# Revit family: ARRN
name_source: partatom
category: Lighting Fixtures
revit_build: Autodesk Revit 2014 (Build: 20130308_1515(x64)
units: mm (PartAtom-declared; Revit-internal decimal feet)

## types (1)
- EVOD
    Apparent Load = 150 VA
    Assembly Code = D5020200
    Color Filter = 16777215
    Connector Description = Lighting Connector
    Default Elevation = 1219.2 mm  [stored 4 ft]
    Description = The Evolution is a highly efficient floodlight that combines Ex de protection with optimised utilisation of light through advanced reflector design. The Evolution concept has no exposed flamepaths making the luminaire effectively maintenance free. Access to the lamp and terminal chamber is achieved by the unscrewing of a single captive bolt.
    Dimming Lamp Color Temperature Shift = <None>
    Emit Shape Visible in Rendering = No
    Emit from Rectangle Length = 300 mm
    Emit from Rectangle Width = 295 mm  [stored 0.967848 ft]
    Features = Installation in gas groups
IIA, IIB and IIC
Easy and quick access
for maintenance
Simple, rapid lamp replacement
and flamepath inspection
Reduced maintenance due to
no exposed flamepath
Exceptional photometric
efficiency
Effective light distribution
for many applications
Timed ignitor supplied as standard
    Fixture distribution = Direct
    Glass = Hubbell - Glass
    Height = 520 mm  [stored 1.70604 ft]
    Housing Material = Paint - Hubbell - Light Silver
    IP Rating = IP66/67
    Lamp = LED
    Length = 375 mm  [stored 1.23031 ft]
    Load Classification = Lighting
    Manufacturer = Chalmit
    Model = EVOD
    Mounting = Paint - Hubbell - Light Silver
    Photometric Web File = CHL_EVPD_250_MS HPS.ies
    Power Factor = 1
    Product Documentation Link = https://hubbellcdn.com
    Product Link = https://www.hubbell.com
    Reflector Finish = Hubbell - White Glass
    Tilt Angle = 0.00°
    URL = https://www.hubbell.com
    Voltage = 120 V
    Warranty = 5 years Warranty
    Wattage Comments = 150W
    Watts = 150 W
    Width = 280 mm  [stored 0.918635 ft]
    Wings = Paint - Hubbell - Light Silver

note: [stored X ft] marks values corroborated as IEEE doubles in the binary element streams (Revit-internal decimal feet)

## geometry (parser evidence)
native form markers: Sweep x2
no freeform markers — native parametric forms only
